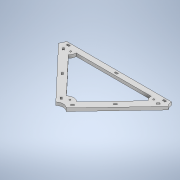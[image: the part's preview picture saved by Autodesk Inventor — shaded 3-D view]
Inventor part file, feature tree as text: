
AUTODESK INVENTOR PART (.ipt)
format: ipt  version: 2020 (Build 240168000, 168)  size: 167,936 bytes
history: native  units: in
note: dims shown in document units (in); Inventor stores cm internally (conversion verified against a paired STEP export)
features: extrude x1, sketch x1
ambient origin geometry x8: Origin, YZ Plane, XZ Plane, XY Plane, X Axis, Y Axis, Z Axis, Center Point
bodies: Solid1 (feature_tree)
feature tree (2):
  extrude  "Extrusion1"  [1 undecoded]
  sketch  "Sketch1"  dims[d0=0.1575in d1=0.0in]
note: 1 required parameter value undecoded (feature->parameter linkage not recoverable at this tier; creation-order binding heuristic only, values carry confidence <= 0.55)
